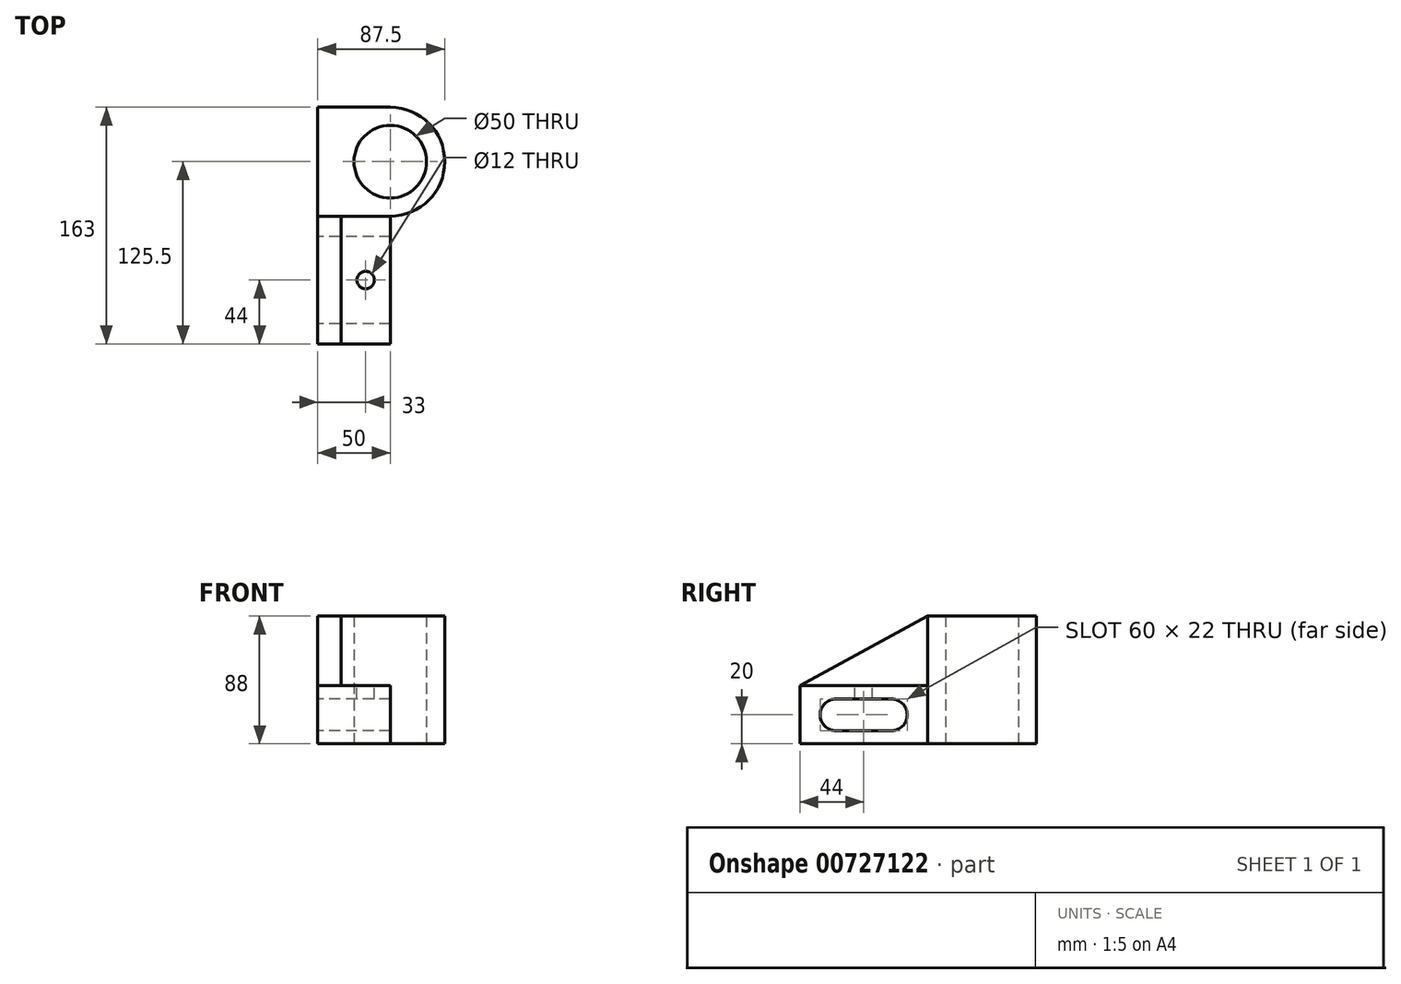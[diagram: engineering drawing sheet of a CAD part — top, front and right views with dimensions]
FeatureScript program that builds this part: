
annotation { "Feature Type Name" : "Feature", "Feature Type Description" : "" }
export const myFeature = defineFeature(function(context is Context, id is Id, definition is map)
    precondition{}
    {
        {
            var Q0;
            Q0=qCreatedBy(makeId("Top.planeOp"),FACE);
            var sketch = newSketch(context, id + "F0", { "sketchPlane" : qUnion([Q0])});
            skLineSegment(sketch, "E0.bottom", {"start": v(0, 0) * mm, "end": v(50, 0) * mm});
            skLineSegment(sketch, "E0.top", {"start": v(0, 75) * mm, "end": v(50, 75) * mm});
            skLineSegment(sketch, "E0.left", {"start": v(0, 0) * mm, "end": v(0, 75) * mm});
            skCircle(sketch, "E1", {"center": v(50, 37.5) * mm, "radius": 25 * mm});
            skArc(sketch, "E2", {"start": v(50, 0) * mm, "mid": v(87.5, 37.5) * mm, "end": v(50, 75) * mm});
            skSolve(sketch);
        }
        {
            var Q0;
            Q0 = qSketchRegion(id + "F0", true);
            extrude(context, id + "F1", {"entities" : qUnion([Q0]), "depth" : 88 * mm, "offsetDistance" : 25 * mm});
        }
        {
            var Q0;
            Q0=qCreatedBy(makeId("Right.planeOp"),FACE);
            var sketch = newSketch(context, id + "F2", { "sketchPlane" : qUnion([Q0])});
            skLineSegment(sketch, "E3.bottom", {"start": v(0, 0) * mm, "end": v(-88, 0) * mm});
            skLineSegment(sketch, "E3.top", {"start": v(0, 40) * mm, "end": v(-88, 40) * mm});
            skLineSegment(sketch, "E3.left", {"start": v(0, 0) * mm, "end": v(0, 40) * mm});
            skLineSegment(sketch, "E3.right", {"start": v(-88, 0) * mm, "end": v(-88, 40) * mm});
            skArc(sketch, "E4", {"start": v(-25, 9) * mm, "mid": v(-14, 20) * mm, "end": v(-25, 31) * mm});
            skArc(sketch, "E5", {"start": v(-63, 31) * mm, "mid": v(-74, 20) * mm, "end": v(-63, 9) * mm});
            skLineSegment(sketch, "E6", {"start": v(-63, 31) * mm, "end": v(-25, 31) * mm});
            skLineSegment(sketch, "E7", {"start": v(-63, 9) * mm, "end": v(-25, 9) * mm});
            skPoint(sketch, "E8.start.orphan", {"position": v(0, 20) * mm});
            skSolve(sketch);
        }
        {
            var Q0;
            Q0 = qSketchRegion(id + "F2", true);
            extrude(context, id + "F3", {"entities" : qUnion([Q0]), "operationType" : NewBodyOperationType.ADD, "depth" : 50 * mm, "offsetDistance" : 25 * mm});
        }
        {
            var Q0;
            Q0=qCreatedBy(makeId("Right.planeOp"),FACE);
            var sketch = newSketch(context, id + "F4", { "sketchPlane" : qUnion([Q0])});
            skLineSegment(sketch, "E9", {"start": v(0, 0) * mm, "end": v(0, 40) * mm});
            skLineSegment(sketch, "E10", {"start": v(0, 40) * mm, "end": v(0, 88) * mm});
            skLineSegment(sketch, "E11", {"start": v(0, 40) * mm, "end": v(-88, 40) * mm});
            skLineSegment(sketch, "E12", {"start": v(0, 88) * mm, "end": v(-88, 40) * mm});
            skSolve(sketch);
        }
        {
            var Q0;
            Q0 = qSketchRegion(id + "F4", true);
            extrude(context, id + "F5", {"entities" : qUnion([Q0]), "operationType" : NewBodyOperationType.ADD, "depth" : 16 * mm, "offsetDistance" : 25 * mm});
        }
        {
            var Q0;
            Q0=makeQuery(id+"F3.opExtrude","SWEPT_FACE",FACE,{"disambiguationData":[OSD([sQuery(id+"F2.wireOp",EDGE,"E3.top")])]});
            var sketch = newSketch(context, id + "F6", { "sketchPlane" : qUnion([Q0])});
            skCircle(sketch, "E13", {"center": v(33, -44) * mm, "radius": 6 * mm});
            skSolve(sketch);
        }
        {
            var Q0;
            Q0 = qSketchRegion(id + "F6", true);
            extrude(context, id + "F7", {"entities" : qUnion([Q0]), "operationType" : NewBodyOperationType.REMOVE, "endBound" : BoundingType.UP_TO_NEXT, "oppositeDirection" : true, "depth" : 25 * mm, "offsetDistance" : 25 * mm});
        }
    });
